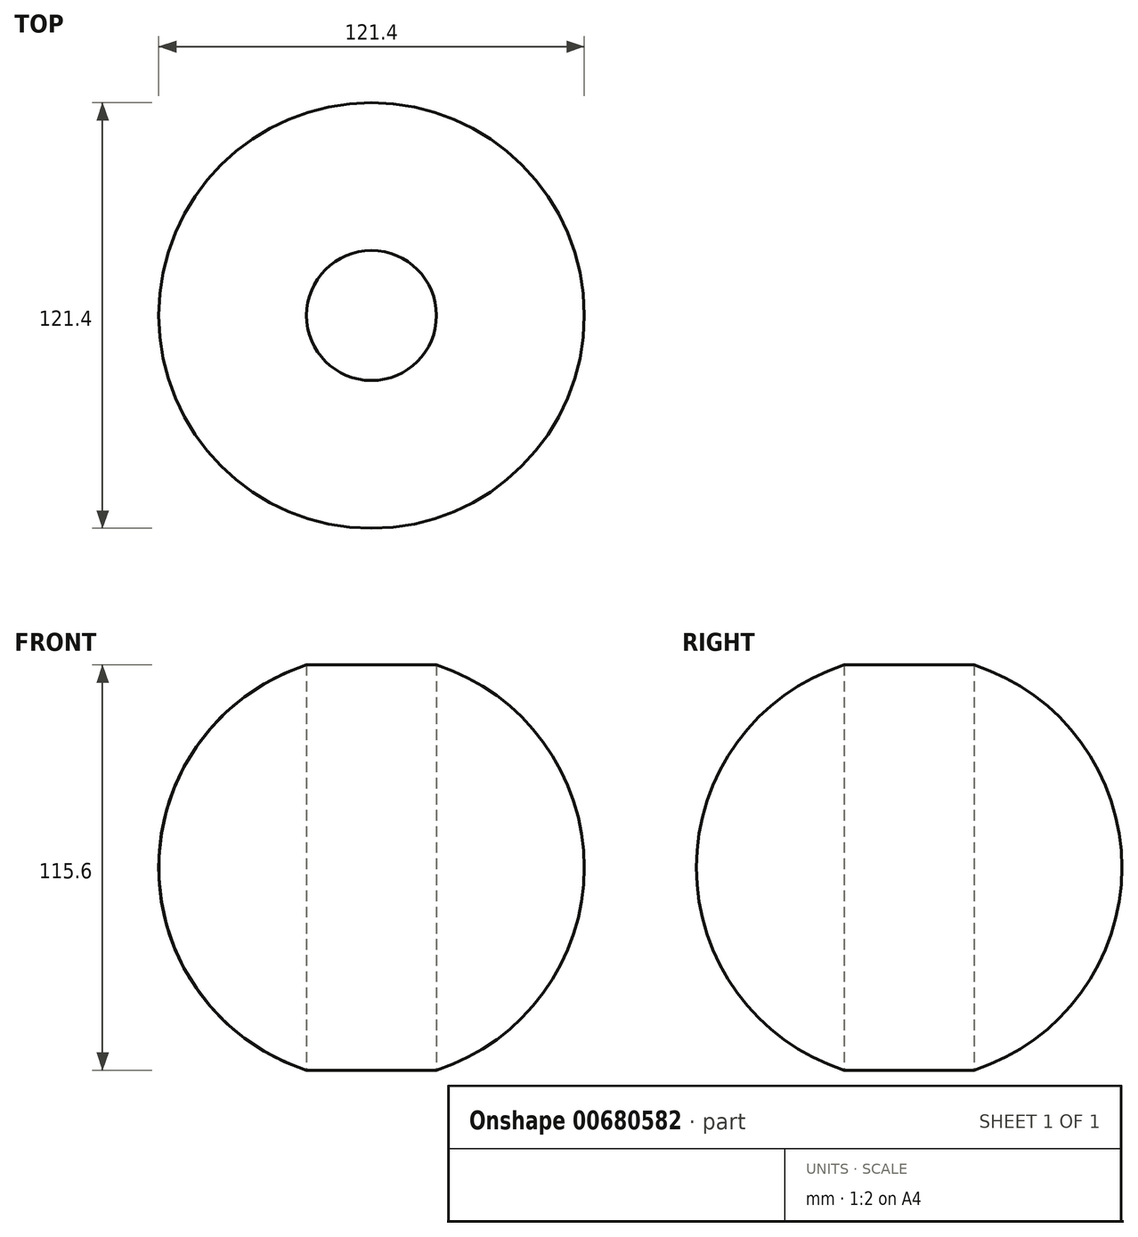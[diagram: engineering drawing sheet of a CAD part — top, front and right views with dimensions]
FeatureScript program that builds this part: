
annotation { "Feature Type Name" : "Feature", "Feature Type Description" : "" }
export const myFeature = defineFeature(function(context is Context, id is Id, definition is map)
    precondition{}
    {
        {
            var Q0;
            Q0=qCreatedBy(makeId("Front.planeOp"),FACE);
            var sketch = newSketch(context, id + "F0", { "sketchPlane" : qUnion([Q0])});
            skArc(sketch, "E0", {"start": v(18.53, -57.8) * mm, "mid": v(60.7, 0) * mm, "end": v(18.53, 57.8) * mm});
            skLineSegment(sketch, "E1", {"start": v(18.53, 57.8) * mm, "end": v(18.53, -57.8) * mm});
            skLineSegment(sketch, "E2", {"start": v(0, 0) * mm, "end": v(0, 54.24) * mm, "construction": true});
            skSolve(sketch);
        }
        {
            var Q0;
            Q0=makeQuery(id+"F0.imprint","IMPRINT",FACE,{"disambiguationData":[TD([[makeQuery(id+"F0.imprint","IMPRINT",EDGE,{"derivedFrom":sQuery(id+"F0.wireOp",EDGE,"E0")}),1.0]])]});
            var Q1;
            Q1=sQuery(id+"F0.wireOp",EDGE,"E2");
            revolve(context, id + "F1", {"entities" : qUnion([Q0]), "axis" : qUnion([Q1]), "revolveType" : RevolveType.FULL});
        }
    });
